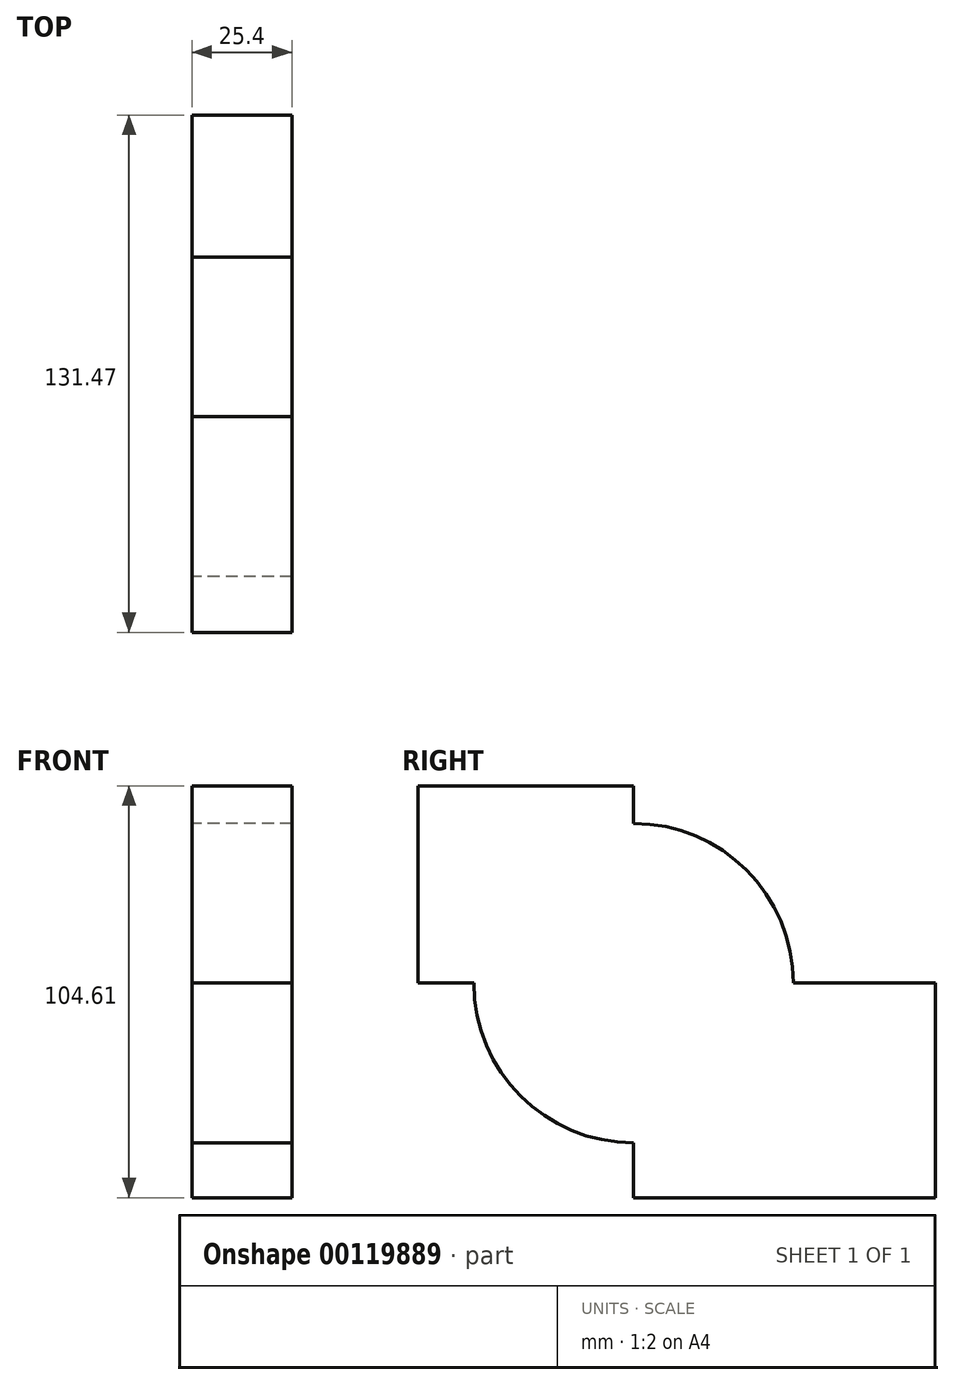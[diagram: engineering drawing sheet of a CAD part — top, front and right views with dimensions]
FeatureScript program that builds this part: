
annotation { "Feature Type Name" : "Feature", "Feature Type Description" : "" }
export const myFeature = defineFeature(function(context is Context, id is Id, definition is map)
    precondition{}
    {
        {
            var Q0;
            Q0=qCreatedBy(makeId("Right.planeOp"),FACE);
            var sketch = newSketch(context, id + "F0", { "sketchPlane" : qUnion([Q0])});
            skCircle(sketch, "E0", {"center": v(0, 0) * mm, "radius": 40.58 * mm});
            skLineSegment(sketch, "E1.bottom", {"start": v(0, 0) * mm, "end": v(-54.78, 0) * mm});
            skLineSegment(sketch, "E1.top", {"start": v(0, 50.1) * mm, "end": v(-54.78, 50.1) * mm});
            skLineSegment(sketch, "E1.left", {"start": v(0, 0) * mm, "end": v(0, 50.1) * mm});
            skLineSegment(sketch, "E1.right", {"start": v(-54.78, 0) * mm, "end": v(-54.78, 50.1) * mm});
            skLineSegment(sketch, "E2.bottom", {"start": v(0, 0) * mm, "end": v(76.7, 0) * mm});
            skLineSegment(sketch, "E2.top", {"start": v(0, -54.51) * mm, "end": v(76.7, -54.51) * mm});
            skLineSegment(sketch, "E2.left", {"start": v(0, 0) * mm, "end": v(0, -54.51) * mm});
            skLineSegment(sketch, "E2.right", {"start": v(76.7, 0) * mm, "end": v(76.7, -54.51) * mm});
            skSolve(sketch);
        }
        {
            var Q0;
            Q0 = qSketchRegion(id + "F0", true);
            extrude(context, id + "F1", {"entities" : qUnion([Q0]), "depth" : 25.4 * mm});
        }
    });
